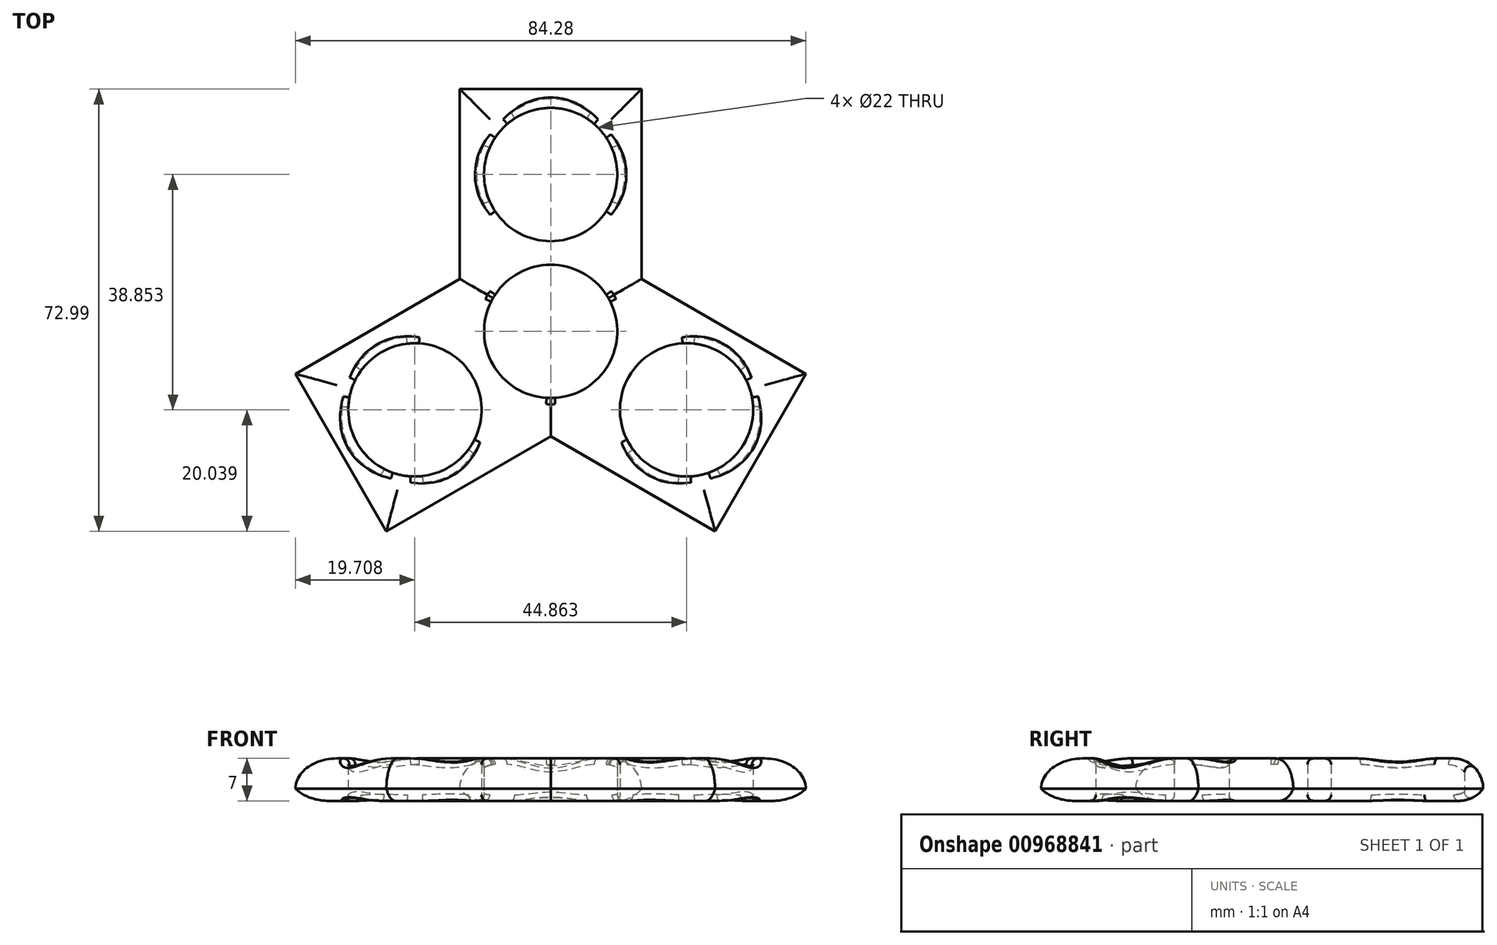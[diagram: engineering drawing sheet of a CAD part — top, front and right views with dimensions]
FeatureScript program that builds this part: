
annotation { "Feature Type Name" : "Feature", "Feature Type Description" : "" }
export const myFeature = defineFeature(function(context is Context, id is Id, definition is map)
    precondition{}
    {
        {
            var Q0;
            Q0=qCreatedBy(makeId("Top.planeOp"),FACE);
            var sketch = newSketch(context, id + "F0", { "sketchPlane" : qUnion([Q0])});
            skCircle(sketch, "E0", {"center": v(0, 0) * mm, "radius": 11 * mm});
            skLineSegment(sketch, "E1.bottom", {"start": v(0, 0) * mm, "end": v(15, 0) * mm});
            skLineSegment(sketch, "E1.top", {"start": v(0, 40) * mm, "end": v(15, 40) * mm});
            skLineSegment(sketch, "E1.left", {"start": v(0, 0) * mm, "end": v(0, 40) * mm});
            skLineSegment(sketch, "E1.right", {"start": v(15, 0) * mm, "end": v(15, 40) * mm});
            skLineSegment(sketch, "E2.bottom", {"start": v(0, 0) * mm, "end": v(-15, 0) * mm});
            skLineSegment(sketch, "E2.top", {"start": v(0, 40) * mm, "end": v(-15, 40) * mm});
            skLineSegment(sketch, "E2.right", {"start": v(-15, 0) * mm, "end": v(-15, 40) * mm});
            skLineSegment(sketch, "E3", {"start": v(0, 40) * mm, "end": v(0, 25.9) * mm});
            skCircle(sketch, "E4", {"center": v(0, 25.9) * mm, "radius": 11 * mm});
            skSolve(sketch);
        }
        {
            var Q0;
            {var subQ0=sQuery(id+"F0.wireOp",EDGE,"E2.top");Q0=makeQuery(id+"F0.imprint","IMPRINT",FACE,{"disambiguationData":[TD([[makeQuery(id+"F0.imprint","IMPRINT",EDGE,{"derivedFrom":subQ0}),1.0]])]});}
            var Q1;
            {var subQ9=sQuery(id+"F0.wireOp",EDGE,"E1.top");Q1=makeQuery(id+"F0.imprint","IMPRINT",FACE,{"disambiguationData":[TD([[makeQuery(id+"F0.imprint","IMPRINT",EDGE,{"derivedFrom":subQ9}),-1.0]])]});}
            extrude(context, id + "F1", {"entities" : qUnion([Q0, Q1]), "depth" : 7 * mm, "offsetDistance" : 25 * mm});
        }
        {
            var Q0;
            Q0=qCreatedBy(makeId("Front.planeOp"),FACE);
            var sketch = newSketch(context, id + "F2", { "sketchPlane" : qUnion([Q0])});
            skLineSegment(sketch, "E5", {"start": v(0, 30.21) * mm, "end": v(0, -19.5) * mm});
            skSolve(sketch);
        }
        {
            var Q0;
            Q0=makeQuery(id+"F1.opExtrude","SWEPT_BODY",BODY,{"disambiguationData":[OSD([sQuery(id+"F0.wireOp",EDGE,"E0"),sQuery(id+"F0.wireOp",EDGE,"E1.bottom"),sQuery(id+"F0.wireOp",EDGE,"E1.top"),sQuery(id+"F0.wireOp",EDGE,"E1.right"),sQuery(id+"F0.wireOp",EDGE,"E2.bottom"),sQuery(id+"F0.wireOp",EDGE,"E2.top"),sQuery(id+"F0.wireOp",EDGE,"E2.right"),sQuery(id+"F0.wireOp",EDGE,"E4")])]});
            var Q1;
            Q1=sQuery(id+"F2.wireOp",EDGE,"E5");
            var Q2;
            Q2=sQuery(id+"F2.wireOp",EDGE,"E5");
            transform(context, id + "F3", {"entities" : qUnion([Q0]), "transformType" : TransformType.ROTATION, "transformAxis" : qUnion([Q2]), "angle" : 120 * degree, "makeCopy" : true});
        }
        {
            var Q0;
            Q0=makeQuery(id+"F1.opExtrude","SWEPT_BODY",BODY,{"disambiguationData":[OSD([sQuery(id+"F0.wireOp",EDGE,"E0"),sQuery(id+"F0.wireOp",EDGE,"E1.bottom"),sQuery(id+"F0.wireOp",EDGE,"E1.top"),sQuery(id+"F0.wireOp",EDGE,"E1.right"),sQuery(id+"F0.wireOp",EDGE,"E2.bottom"),sQuery(id+"F0.wireOp",EDGE,"E2.top"),sQuery(id+"F0.wireOp",EDGE,"E2.right"),sQuery(id+"F0.wireOp",EDGE,"E4")])]});
            var Q1;
            Q1=sQuery(id+"F2.wireOp",EDGE,"E5");
            transform(context, id + "F4", {"entities" : qUnion([Q0]), "transformType" : TransformType.ROTATION, "transformAxis" : qUnion([Q1]), "angle" : 240 * degree, "makeCopy" : true});
        }
        {
            var Q0;
            Q0=makeQuery(id+"F1.opExtrude","SWEPT_BODY",BODY,{"disambiguationData":[OSD([sQuery(id+"F0.wireOp",EDGE,"E0"),sQuery(id+"F0.wireOp",EDGE,"E1.bottom"),sQuery(id+"F0.wireOp",EDGE,"E1.top"),sQuery(id+"F0.wireOp",EDGE,"E1.right"),sQuery(id+"F0.wireOp",EDGE,"E2.bottom"),sQuery(id+"F0.wireOp",EDGE,"E2.top"),sQuery(id+"F0.wireOp",EDGE,"E2.right"),sQuery(id+"F0.wireOp",EDGE,"E4")])]});
            var Q1;
            Q1=makeQuery(id+"F4.opPattern","COPY",BODY,{"derivedFrom":makeQuery(id+"F1.opExtrude","SWEPT_BODY",BODY,{"disambiguationData":[OSD([sQuery(id+"F0.wireOp",EDGE,"E0"),sQuery(id+"F0.wireOp",EDGE,"E1.bottom"),sQuery(id+"F0.wireOp",EDGE,"E1.top"),sQuery(id+"F0.wireOp",EDGE,"E1.right"),sQuery(id+"F0.wireOp",EDGE,"E2.bottom"),sQuery(id+"F0.wireOp",EDGE,"E2.top"),sQuery(id+"F0.wireOp",EDGE,"E2.right"),sQuery(id+"F0.wireOp",EDGE,"E4")])]}),"instanceName":"1"});
            var Q2;
            Q2=makeQuery(id+"F3.opPattern","COPY",BODY,{"derivedFrom":makeQuery(id+"F1.opExtrude","SWEPT_BODY",BODY,{"disambiguationData":[OSD([sQuery(id+"F0.wireOp",EDGE,"E0"),sQuery(id+"F0.wireOp",EDGE,"E1.bottom"),sQuery(id+"F0.wireOp",EDGE,"E1.top"),sQuery(id+"F0.wireOp",EDGE,"E1.right"),sQuery(id+"F0.wireOp",EDGE,"E2.bottom"),sQuery(id+"F0.wireOp",EDGE,"E2.top"),sQuery(id+"F0.wireOp",EDGE,"E2.right"),sQuery(id+"F0.wireOp",EDGE,"E4")])]}),"instanceName":"1"});
            booleanBodies(context, id + "F5", {"operationType" : BooleanOperationType.UNION, "tools" : qUnion([Q0, Q1, Q2])});
        }
        {
            var Q0;
            Q0=makeQuery(id+"F1.opExtrude","CAP_EDGE",EDGE,{"disambiguationData":[OSD([sQuery(id+"F0.wireOp",EDGE,"E1.right")])],"isStart":false});
            var Q1;
            Q1=makeQuery(id+"F3.opPattern","COPY",EDGE,{"derivedFrom":makeQuery(id+"F1.opExtrude","CAP_EDGE",EDGE,{"disambiguationData":[OSD([sQuery(id+"F0.wireOp",EDGE,"E2.right")])],"isStart":false}),"instanceName":"1"});
            var Q2;
            Q2=makeQuery(id+"F3.opPattern","COPY",EDGE,{"derivedFrom":makeQuery(id+"F1.opExtrude","CAP_EDGE",EDGE,{"disambiguationData":[OSD([sQuery(id+"F0.wireOp",EDGE,"E1.top"),sQuery(id+"F0.wireOp",EDGE,"E2.top")])],"isStart":false}),"instanceName":"1"});
            var Q3;
            Q3=makeQuery(id+"F3.opPattern","COPY",EDGE,{"derivedFrom":makeQuery(id+"F1.opExtrude","CAP_EDGE",EDGE,{"disambiguationData":[OSD([sQuery(id+"F0.wireOp",EDGE,"E1.right")])],"isStart":false}),"instanceName":"1"});
            var Q4;
            Q4=makeQuery(id+"F4.opPattern","COPY",EDGE,{"derivedFrom":makeQuery(id+"F1.opExtrude","CAP_EDGE",EDGE,{"disambiguationData":[OSD([sQuery(id+"F0.wireOp",EDGE,"E2.right")])],"isStart":false}),"instanceName":"1"});
            var Q5;
            Q5=makeQuery(id+"F4.opPattern","COPY",EDGE,{"derivedFrom":makeQuery(id+"F1.opExtrude","CAP_EDGE",EDGE,{"disambiguationData":[OSD([sQuery(id+"F0.wireOp",EDGE,"E1.top"),sQuery(id+"F0.wireOp",EDGE,"E2.top")])],"isStart":false}),"instanceName":"1"});
            var Q6;
            Q6=makeQuery(id+"F4.opPattern","COPY",EDGE,{"derivedFrom":makeQuery(id+"F1.opExtrude","CAP_EDGE",EDGE,{"disambiguationData":[OSD([sQuery(id+"F0.wireOp",EDGE,"E1.right")])],"isStart":false}),"instanceName":"1"});
            var Q7;
            Q7=makeQuery(id+"F1.opExtrude","CAP_EDGE",EDGE,{"disambiguationData":[OSD([sQuery(id+"F0.wireOp",EDGE,"E2.right")])],"isStart":false});
            var Q8;
            Q8=makeQuery(id+"F1.opExtrude","CAP_EDGE",EDGE,{"disambiguationData":[OSD([sQuery(id+"F0.wireOp",EDGE,"E1.top"),sQuery(id+"F0.wireOp",EDGE,"E2.top")])],"isStart":false});
            fillet(context, id + "F6", {"entities" : qUnion([Q0, Q1, Q2, Q3, Q4, Q5, Q6, Q7, Q8]), "radius" : 5 * mm, "tangentPropagation" : true, "allowEdgeOverflow" : false});
        }
        {
            var Q0;
            Q0=makeQuery(id+"F4.opPattern","COPY",EDGE,{"derivedFrom":makeQuery(id+"F1.opExtrude","CAP_EDGE",EDGE,{"disambiguationData":[OSD([sQuery(id+"F0.wireOp",EDGE,"E1.right")])],"isStart":true}),"instanceName":"1"});
            var Q1;
            Q1=makeQuery(id+"F4.opPattern","COPY",EDGE,{"derivedFrom":makeQuery(id+"F1.opExtrude","CAP_EDGE",EDGE,{"disambiguationData":[OSD([sQuery(id+"F0.wireOp",EDGE,"E1.top"),sQuery(id+"F0.wireOp",EDGE,"E2.top")])],"isStart":true}),"instanceName":"1"});
            var Q2;
            Q2=makeQuery(id+"F4.opPattern","COPY",EDGE,{"derivedFrom":makeQuery(id+"F1.opExtrude","CAP_EDGE",EDGE,{"disambiguationData":[OSD([sQuery(id+"F0.wireOp",EDGE,"E2.right")])],"isStart":true}),"instanceName":"1"});
            var Q3;
            Q3=makeQuery(id+"F3.opPattern","COPY",EDGE,{"derivedFrom":makeQuery(id+"F1.opExtrude","CAP_EDGE",EDGE,{"disambiguationData":[OSD([sQuery(id+"F0.wireOp",EDGE,"E1.right")])],"isStart":true}),"instanceName":"1"});
            var Q4;
            Q4=makeQuery(id+"F3.opPattern","COPY",EDGE,{"derivedFrom":makeQuery(id+"F1.opExtrude","CAP_EDGE",EDGE,{"disambiguationData":[OSD([sQuery(id+"F0.wireOp",EDGE,"E1.top"),sQuery(id+"F0.wireOp",EDGE,"E2.top")])],"isStart":true}),"instanceName":"1"});
            var Q5;
            Q5=makeQuery(id+"F3.opPattern","COPY",EDGE,{"derivedFrom":makeQuery(id+"F1.opExtrude","CAP_EDGE",EDGE,{"disambiguationData":[OSD([sQuery(id+"F0.wireOp",EDGE,"E2.right")])],"isStart":true}),"instanceName":"1"});
            var Q6;
            Q6=makeQuery(id+"F1.opExtrude","CAP_EDGE",EDGE,{"disambiguationData":[OSD([sQuery(id+"F0.wireOp",EDGE,"E1.right")])],"isStart":true});
            var Q7;
            Q7=makeQuery(id+"F1.opExtrude","CAP_EDGE",EDGE,{"disambiguationData":[OSD([sQuery(id+"F0.wireOp",EDGE,"E1.top"),sQuery(id+"F0.wireOp",EDGE,"E2.top")])],"isStart":true});
            var Q8;
            Q8=makeQuery(id+"F1.opExtrude","CAP_EDGE",EDGE,{"disambiguationData":[OSD([sQuery(id+"F0.wireOp",EDGE,"E2.right")])],"isStart":true});
            fillet(context, id + "F7", {"entities" : qUnion([Q0, Q1, Q2, Q3, Q4, Q5, Q6, Q7, Q8]), "radius" : 5 * mm, "tangentPropagation" : true, "allowEdgeOverflow" : false});
        }
        {
            var Q0;
            Q0=makeQuery(id+"F1.opExtrude","SWEPT_FACE",FACE,{"disambiguationData":[OSD([sQuery(id+"F0.wireOp",EDGE,"E4")])]});
            var Q1;
            {var subQ0=makeQuery(id+"F1.opExtrude","SWEPT_FACE",FACE,{"disambiguationData":[OSD([sQuery(id+"F0.wireOp",EDGE,"E0")])]});Q1=makeQuery(id+"F5.opBoolean","MERGE",FACE,{"derivedFrom":[subQ0,makeQuery(id+"F3.opPattern","COPY",FACE,{"derivedFrom":subQ0,"instanceName":"1"}),makeQuery(id+"F4.opPattern","COPY",FACE,{"derivedFrom":subQ0,"instanceName":"1"})]});}
            var Q2;
            Q2=makeQuery(id+"F4.opPattern","COPY",FACE,{"derivedFrom":makeQuery(id+"F1.opExtrude","SWEPT_FACE",FACE,{"disambiguationData":[OSD([sQuery(id+"F0.wireOp",EDGE,"E4")])]}),"instanceName":"1"});
            var Q3;
            Q3=makeQuery(id+"F3.opPattern","COPY",FACE,{"derivedFrom":makeQuery(id+"F1.opExtrude","SWEPT_FACE",FACE,{"disambiguationData":[OSD([sQuery(id+"F0.wireOp",EDGE,"E4")])]}),"instanceName":"1"});
            fillet(context, id + "F8", {"entities" : qUnion([Q0, Q1, Q2, Q3]), "radius" : 1 * mm, "allowEdgeOverflow" : false});
        }
    });
